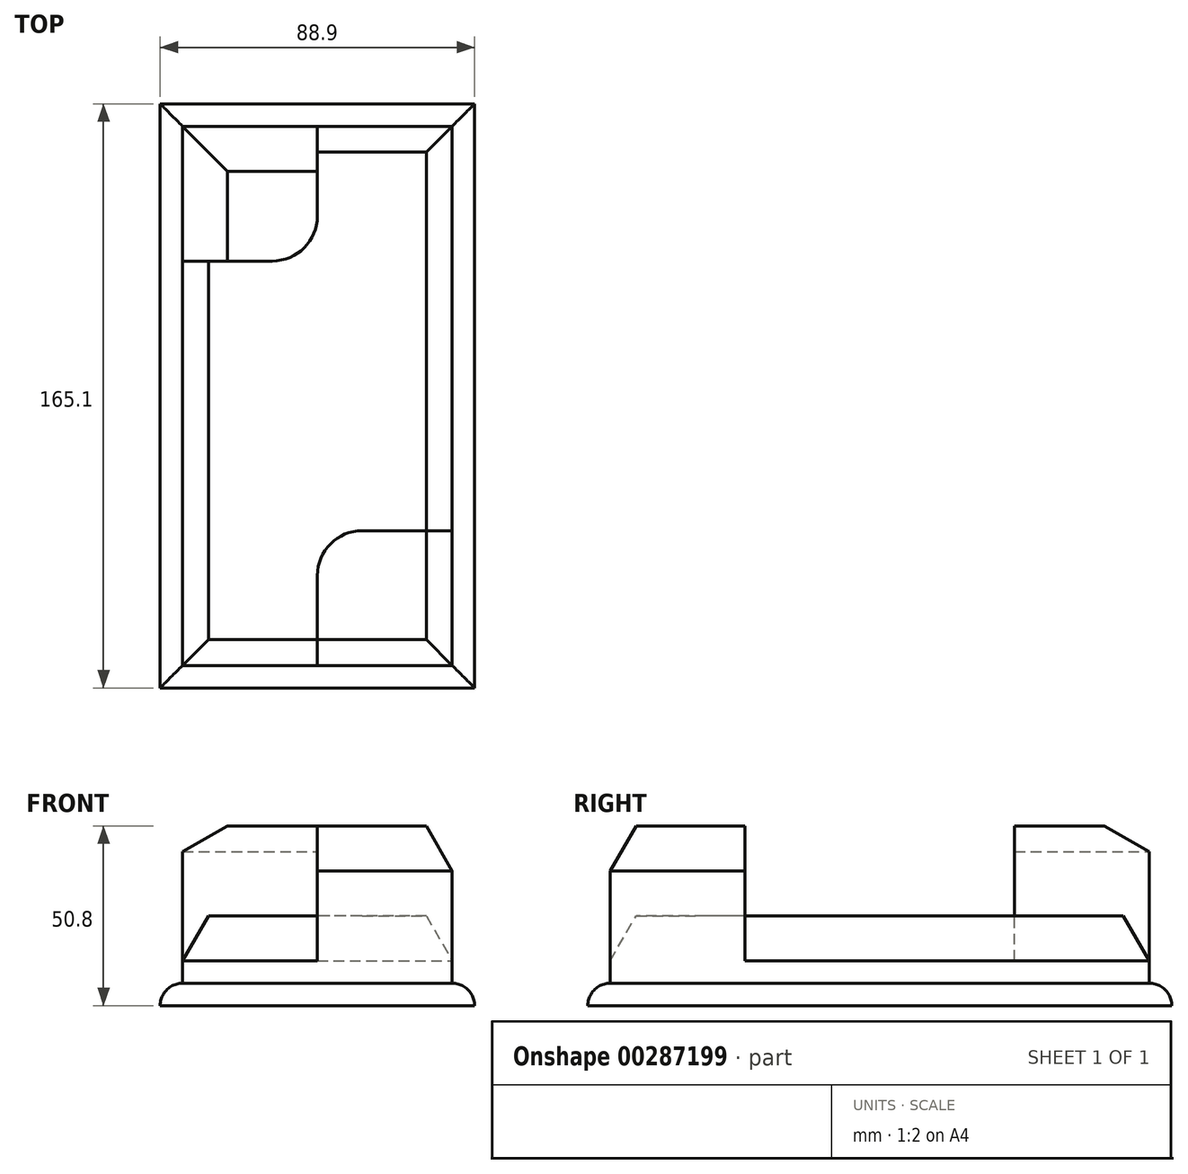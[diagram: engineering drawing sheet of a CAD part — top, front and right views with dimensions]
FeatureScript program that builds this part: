
annotation { "Feature Type Name" : "Feature", "Feature Type Description" : "" }
export const myFeature = defineFeature(function(context is Context, id is Id, definition is map)
    precondition{}
    {
        {
            var Q0;
            Q0=qCreatedBy(makeId("Top.planeOp"),FACE);
            var sketch = newSketch(context, id + "F0", { "sketchPlane" : qUnion([Q0])});
            skPoint(sketch, "E0.middle", {"position": v(0, 0) * mm});
            skLineSegment(sketch, "E1.bottom", {"start": v(38.1, 76.2) * mm, "end": v(-38.1, 76.2) * mm});
            skLineSegment(sketch, "E1.top", {"start": v(38.1, -76.2) * mm, "end": v(-38.1, -76.2) * mm});
            skLineSegment(sketch, "E1.left", {"start": v(38.1, 76.2) * mm, "end": v(38.1, -76.2) * mm});
            skLineSegment(sketch, "E1.right", {"start": v(-38.1, 76.2) * mm, "end": v(-38.1, -76.2) * mm});
            skLineSegment(sketch, "E2", {"start": v(0, 76.2) * mm, "end": v(0, 50.8) * mm});
            skLineSegment(sketch, "E3", {"start": v(-12.7, 38.1) * mm, "end": v(-38.1, 38.1) * mm});
            skLineSegment(sketch, "E4", {"start": v(0, -76.2) * mm, "end": v(0, -50.8) * mm});
            skLineSegment(sketch, "E5", {"start": v(12.7, -38.1) * mm, "end": v(38.1, -38.1) * mm});
            skPoint(sketch, "E6.visualSharp", {"position": v(0, 38.1) * mm});
            skArc(sketch, "E6.filletArc", {"start": v(-12.7, 38.1) * mm, "mid": v(-3.72, 41.82) * mm, "end": v(0, 50.8) * mm});
            skPoint(sketch, "E7.visualSharp", {"position": v(0, -38.1) * mm});
            skArc(sketch, "E7.filletArc", {"start": v(12.7, -38.1) * mm, "mid": v(3.72, -41.82) * mm, "end": v(0, -50.8) * mm});
            skLineSegment(sketch, "E8.0", {"start": v(44.45, 82.55) * mm, "end": v(-44.45, 82.55) * mm});
            skLineSegment(sketch, "E8.1", {"start": v(44.45, 82.55) * mm, "end": v(44.45, -82.55) * mm});
            skLineSegment(sketch, "E8.2", {"start": v(44.45, -82.55) * mm, "end": v(-44.45, -82.55) * mm});
            skLineSegment(sketch, "E8.3", {"start": v(-44.45, 82.55) * mm, "end": v(-44.45, -82.55) * mm});
            skSolve(sketch);
        }
        {
            var Q0;
            Q0=makeQuery(id+"F0.imprint","IMPRINT",FACE,{"disambiguationData":[TD([[makeQuery(id+"F0.imprint","IMPRINT",EDGE,{"derivedFrom":sQuery(id+"F0.wireOp",EDGE,"E8.0")}),1.0]])]});
            extrude(context, id + "F1", {"entities" : qUnion([Q0]), "depth" : 6.35 * mm});
        }
        {
            var Q0;
            {var subQ9=sQuery(id+"F0.wireOp",EDGE,"E2");Q0=makeQuery(id+"F0.imprint","IMPRINT",FACE,{"disambiguationData":[TD([[makeQuery(id+"F0.imprint","IMPRINT",EDGE,{"derivedFrom":subQ9}),1.0]])]});}
            extrude(context, id + "F2", {"entities" : qUnion([Q0]), "operationType" : NewBodyOperationType.ADD, "depth" : 25.4 * mm});
        }
        {
            var Q0;
            {var subQ1=sQuery(id+"F0.wireOp",EDGE,"E2");Q0=makeQuery(id+"F0.imprint","IMPRINT",FACE,{"disambiguationData":[TD([[makeQuery(id+"F0.imprint","IMPRINT",EDGE,{"derivedFrom":subQ1}),-1.0]])]});}
            var Q1;
            {var subQ1=sQuery(id+"F0.wireOp",EDGE,"E4");Q1=makeQuery(id+"F0.imprint","IMPRINT",FACE,{"disambiguationData":[TD([[makeQuery(id+"F0.imprint","IMPRINT",EDGE,{"derivedFrom":subQ1}),-1.0]])]});}
            extrude(context, id + "F3", {"entities" : qUnion([Q0, Q1]), "operationType" : NewBodyOperationType.ADD, "depth" : 50.8 * mm});
        }
        {
            var Q0;
            Q0=makeQuery(id+"F2.opExtrude","CAP_EDGE",EDGE,{"disambiguationData":[OSD([sQuery(id+"F0.wireOp",EDGE,"E1.top")])],"isStart":false});
            var Q1;
            Q1=makeQuery(id+"F3.opExtrude","CAP_EDGE",EDGE,{"disambiguationData":[OSD([sQuery(id+"F0.wireOp",EDGE,"E1.top")])],"isStart":false});
            var Q2;
            Q2=makeQuery(id+"F2.opExtrude","CAP_EDGE",EDGE,{"disambiguationData":[OSD([sQuery(id+"F0.wireOp",EDGE,"E1.right")])],"isStart":false});
            var Q3;
            Q3=makeQuery(id+"F2.opExtrude","CAP_EDGE",EDGE,{"disambiguationData":[OSD([sQuery(id+"F0.wireOp",EDGE,"E1.left")])],"isStart":false});
            var Q4;
            Q4=makeQuery(id+"F2.opExtrude","CAP_EDGE",EDGE,{"disambiguationData":[OSD([sQuery(id+"F0.wireOp",EDGE,"E1.bottom")])],"isStart":false});
            var Q5;
            Q5=makeQuery(id+"F3.opExtrude","CAP_EDGE",EDGE,{"disambiguationData":[OSD([sQuery(id+"F0.wireOp",EDGE,"E1.bottom")])],"isStart":false});
            var Q6;
            Q6=makeQuery(id+"F3.opExtrude","CAP_EDGE",EDGE,{"disambiguationData":[OSD([sQuery(id+"F0.wireOp",EDGE,"E1.right")])],"isStart":false});
            var Q7;
            Q7=makeQuery(id+"F3.opExtrude","CAP_EDGE",EDGE,{"disambiguationData":[OSD([sQuery(id+"F0.wireOp",EDGE,"E1.left")])],"isStart":false});
            chamfer(context, id + "F4", {"entities" : qUnion([Q0, Q1, Q2, Q3, Q4, Q5, Q6, Q7]), "chamferType" : ChamferType.OFFSET_ANGLE, "width" : 12.7 * mm, "oppositeDirection" : false, "angle" : 30 * degree, "tangentPropagation" : true});
        }
        {
            var Q0;
            Q0=makeQuery(id+"F1.opExtrude","CAP_EDGE",EDGE,{"disambiguationData":[OSD([sQuery(id+"F0.wireOp",EDGE,"E8.1")])],"isStart":false});
            var Q1;
            Q1=makeQuery(id+"F1.opExtrude","CAP_EDGE",EDGE,{"disambiguationData":[OSD([sQuery(id+"F0.wireOp",EDGE,"E8.0")])],"isStart":false});
            var Q2;
            Q2=makeQuery(id+"F1.opExtrude","CAP_EDGE",EDGE,{"disambiguationData":[OSD([sQuery(id+"F0.wireOp",EDGE,"E8.2")])],"isStart":false});
            var Q3;
            Q3=makeQuery(id+"F1.opExtrude","CAP_EDGE",EDGE,{"disambiguationData":[OSD([sQuery(id+"F0.wireOp",EDGE,"E8.3")])],"isStart":false});
            fillet(context, id + "F5", {"entities" : qUnion([Q0, Q1, Q2, Q3]), "radius" : 6.35 * mm, "tangentPropagation" : true, "allowEdgeOverflow" : false});
        }
    });
